# Revit family: Spino
name_source: partatom
category: Мебель
revit_build: Autodesk Revit 2017 (Build: 20160225_1515(x64)
units: mm (PartAtom-declared; Revit-internal decimal feet)

## family parameters
Всегда вертикально = Да
Заголовок OmniClass = General Furniture and Specialties
На основе рабочей плоскости = Нет
Номер OmniClass = 23.40.20.00
Общий = Нет
При загрузке вырезать с полостями = Нет
Точка расчета площади = Нет

## types (12) — shared parameters
Legs Material = Skandiform Chrome
Seat Material = Skandiform Fabric
Изготовитель = Skandiform AB
Ключевая пометка = XBF.4
Комментарии к типоразмеру = Created by Astacus AB

## per-type parameters (varying)
| type | Leg | Rest In | Rest Out | Seat | URL |
| SA-335 | 1 | 0 | 0 | 1 | www.biminfo.se/?productid=333367 |
| SA-336 | 1 | 1 | 0 | 0 | http://file-system.ru |
| SA-337 | 1 | 0 | 1 | 0 | www.biminfo.se/?productid=333367 |
| SA-340 | 0 | 0 | 0 | 1 | www.biminfo.se/?productid=333367 |
| SA-341 | 0 | 0 | 0 | 1 | www.biminfo.se/?productid=333367 |
| SA-342 | 0 | 0 | 0 | 1 | www.biminfo.se/?productid=333367 |
| SA-343 | 0 | 1 | 0 | 0 | www.biminfo.se/?productid=333367 |
| SA-344 | 0 | 1 | 0 | 0 | www.biminfo.se/?productid=333367 |
| SA-345 | 0 | 1 | 0 | 0 | www.biminfo.se/?productid=333367 |
| SA-346 | 0 | 0 | 1 | 0 | www.biminfo.se/?productid=333367 |
| SA-347 | 0 | 0 | 1 | 0 | www.biminfo.se/?productid=333367 |
| SA-348 | 0 | 0 | 1 | 0 | www.biminfo.se/?productid=333367 |

note: column(s) folded — value = type name in every type: Группа модели

## geometry (parser evidence)
native form markers: Blend x32, Sweep x5
no freeform markers — native parametric forms only
